# Revit family: FU_Table_Sandler_FLOE 0210
name_source: partatom
category: Furniture
units: mm (PartAtom-declared; Revit-internal decimal feet)

## family parameters
Always vertical = Yes
Cut with Voids When Loaded = No
OmniClass Number = 23.40.20.00
OmniClass Title = General Furniture and Specialties
Render Appearance Source = Family Geometry
Room Calculation Point = No
Shared = No
Work Plane-Based = No

## types (2) — shared parameters
Depth = 400 mm  [stored 1.31234 ft]
Description = Height-adjustable side table with 40cm/15.7" square tabletop. Using the gas lift column, the height ranges from 55cm/21.7" to 77cm/30.3". Aluminum base. Plastic glides as standard. Designed by Pearson Lloyd.
Height = 550 mm  [stored 1.80446 ft]
Manufacturer = Sandler
Max Height = 770 mm  [stored 2.52625 ft]
Min Height = 550 mm  [stored 1.80446 ft]
Requested Height = 550 mm  [stored 1.80446 ft]
URL = https://www.sandlerseating.com
Width = 400 mm  [stored 1.31234 ft]
zero-valued in all types: Default Elevation

## per-type parameters (varying)
| type | Model | Top Type |
| FLOE 0210 - Wood Top | Floe 0210 | Floe Top Wood : Floe Wood 40 |
| FLOE 0210 - Laminate Top | FLOE 0210 | Floe Top Laminate : Floe Laminate 40 |

note: [stored X ft] marks values corroborated as IEEE doubles in the binary element streams (Revit-internal decimal feet)

## geometry (parser evidence)
native form markers: Sweep x7
no freeform markers — native parametric forms only
